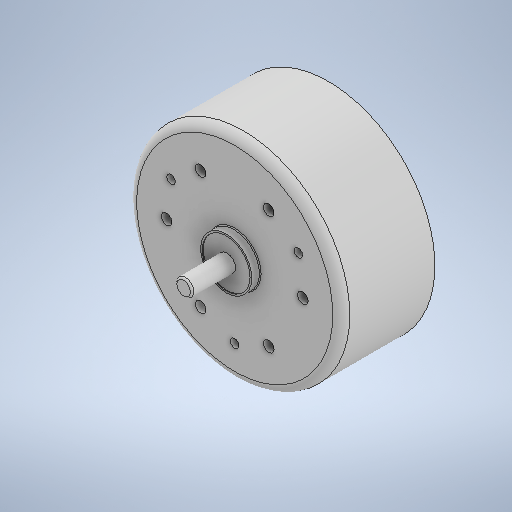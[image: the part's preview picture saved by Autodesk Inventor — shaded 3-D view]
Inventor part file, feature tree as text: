
AUTODESK INVENTOR PART (.ipt)
format: ipt  version: 2025.3 (Build 293356000, 356)  size: 353,792 bytes
history: native  units: mm
features: other x1, fillet x1
ambient origin geometry x8: Origin, YZ Plane, XZ Plane, XY Plane, X Axis, Y Axis, Z Axis, Center Point
bodies: Body1 (feature_tree)
feature tree (2):
  other  "Sólido1"
  fillet  "Fillet6"  [1 undecoded]
note: 1 required parameter value undecoded (feature->parameter linkage not recoverable at this tier; creation-order binding heuristic only, values carry confidence <= 0.55)
